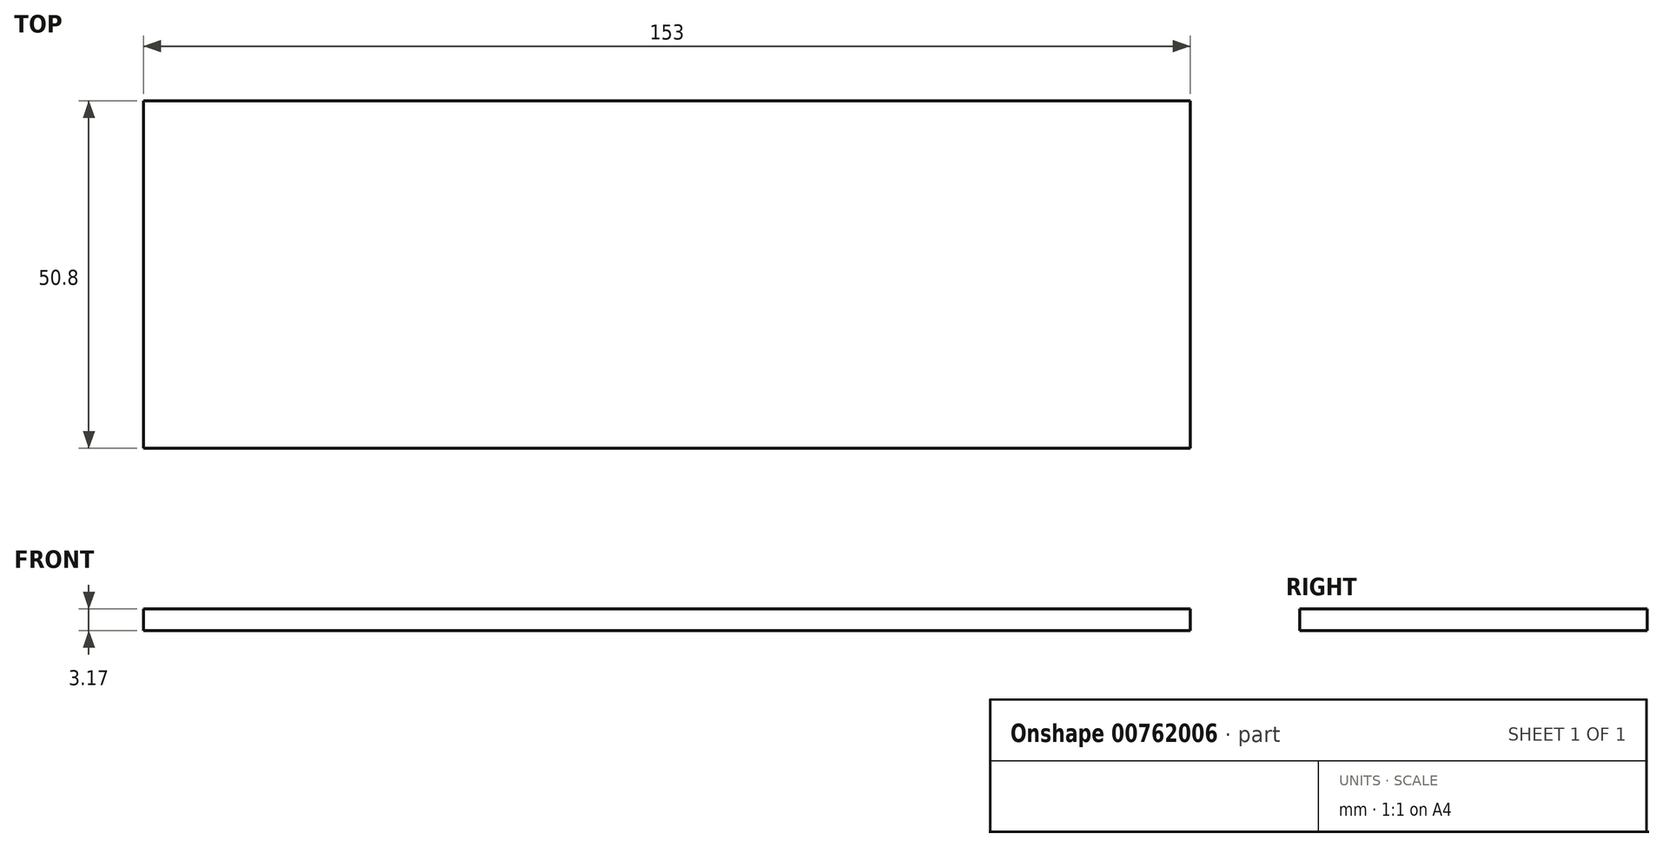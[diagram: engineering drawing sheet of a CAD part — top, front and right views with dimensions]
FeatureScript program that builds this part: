
annotation { "Feature Type Name" : "Feature", "Feature Type Description" : "" }
export const myFeature = defineFeature(function(context is Context, id is Id, definition is map)
    precondition{}
    {
        {
            var Q0;
            Q0=qCreatedBy(makeId("Top.planeOp"),FACE);
            var sketch = newSketch(context, id + "F0", { "sketchPlane" : qUnion([Q0])});
            skLineSegment(sketch, "E0.bottom", {"start": v(-76.5, 25.4) * mm, "end": v(76.5, 25.4) * mm});
            skLineSegment(sketch, "E0.top", {"start": v(-76.5, -25.4) * mm, "end": v(76.5, -25.4) * mm});
            skLineSegment(sketch, "E0.left", {"start": v(-76.5, 25.4) * mm, "end": v(-76.5, -25.4) * mm});
            skLineSegment(sketch, "E0.right", {"start": v(76.5, 25.4) * mm, "end": v(76.5, -25.4) * mm});
            skPoint(sketch, "E0.middle", {"position": v(0, 0) * mm});
            skSolve(sketch);
        }
        {
            var Q0;
            Q0 = qSketchRegion(id + "F0", true);
            extrude(context, id + "F1", {"entities" : qUnion([Q0]), "depth" : 3.17 * mm, "offsetDistance" : 25.4 * mm});
        }
    });
